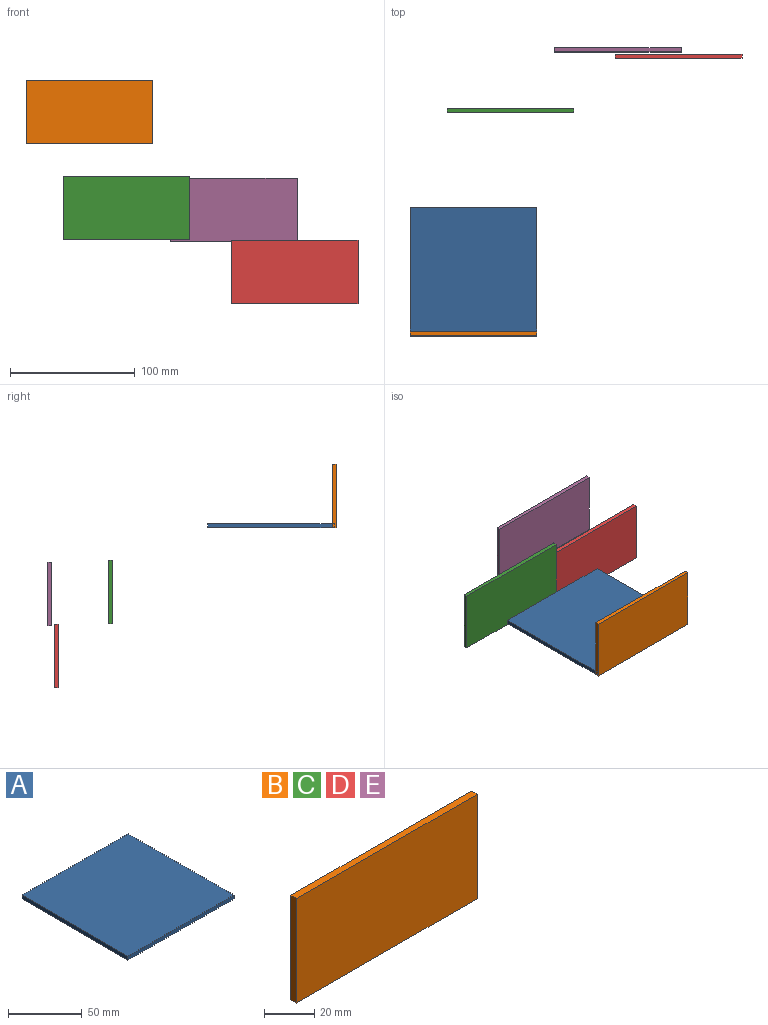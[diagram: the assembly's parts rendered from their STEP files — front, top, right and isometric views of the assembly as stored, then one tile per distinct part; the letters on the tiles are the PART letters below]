
ASSEMBLY  parts=5 mates=1
PART A: 6 faces, bbox 101.6x101.6x3.2 mm
  f0: plane 101.6x3.18mm, normal (-1,0,0), area 322.6mm2, adj f1,f3,f4,f5
  f1: plane 101.6x3.18mm, normal (0,-1,0), area 322.6mm2, adj f0,f2,f4,f5
  f2: plane 101.6x3.18mm, normal (1,0,0), area 322.6mm2, adj f1,f3,f4,f5
  f3: plane 101.6x3.18mm, normal (0,1,0), area 322.6mm2, adj f0,f2,f4,f5
  f4: plane 101.6x101.6mm, normal (0,0,1), area 10322.6mm2, adj f0,f1,f2,f3
  f5: plane 101.6x101.6mm, normal (0,0,-1), area 10322.6mm2, adj f0,f1,f2,f3
PART B: 6 faces, bbox 101.6x3.2x50.8 mm
  f0: plane 101.6x3.18mm, normal (0,0,1), area 322.6mm2, adj f1,f3,f4,f5
  f1: plane 50.8x3.18mm, normal (-1,0,0), area 161.3mm2, adj f0,f2,f4,f5
  f2: plane 101.6x3.18mm, normal (0,0,-1), area 322.6mm2, adj f1,f3,f4,f5
  f3: plane 50.8x3.18mm, normal (1,0,0), area 161.3mm2, adj f0,f2,f4,f5
  f4: plane 101.6x50.8mm, normal (0,-1,0), area 5161.3mm2, adj f0,f1,f2,f3
  f5: plane 101.6x50.8mm, normal (0,1,0), area 5161.3mm2, adj f0,f1,f2,f3
PART C: same geometry as B
PART D: same geometry as B
PART E: same geometry as B
PLACE A t=(-95.07,-154.12,85.34)mm
PLACE B t=(-69.01,-193.77,84.12)mm
PLACE C t=(-39.01,-14.31,7.06)mm
PLACE D t=(95.97,29.34,-44.36)mm
PLACE E t=(47.1,34.37,5.51)mm
MATE fastened B.f2 <-> A.f5  axis (0,0,-1) through (-96.43,-195.35,85.34)mm
